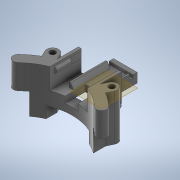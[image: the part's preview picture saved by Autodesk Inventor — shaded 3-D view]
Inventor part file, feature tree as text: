
AUTODESK INVENTOR PART (.ipt)
format: ipt  version: 2020 (Build 240168000, 168)  size: 684,544 bytes
history: native  units: mm
features: extrude x18, sketch x17, projected_geometry x14, other x6, sweep x1, chamfer x1
ambient origin geometry x8: Origin, YZ Plane, XZ Plane, XY Plane, X Axis, Y Axis, Z Axis, Center Point
bodies: Body1 (feature_tree)
feature tree (57):
  other  "Твердое тело1"
  extrude  "Выдавливание1"  Depth=35.0mm TaperAngle=0.0deg
  sketch  "Эскиз2"
  extrude  "Выдавливание2"  Depth=4.0mm
  sweep  "Сдвиг1"
  extrude  "Выдавливание5"  Depth=8.0mm
  extrude  "Выдавливание6"  Depth=35.0mm TaperAngle=0.0deg
  extrude  "Выдавливание7"  Depth=8.5mm
  extrude  "Выдавливание8"  TaperAngle=45.0deg  [1 undecoded]
  other  "РабПлоскость1"
  extrude  "Выдавливание9"  Depth=8.5mm
  extrude  "Выдавливание10"  TaperAngle=45.0deg  [1 undecoded]
  extrude  "Выдавливание11"  TaperAngle=0.0deg  [1 undecoded]
  sketch  "Эскиз13"
  other  "РабПлоскость2"
  sketch  "Эскиз14"
  extrude  "Выдавливание12"  Depth=5.0mm TaperAngle=0.0deg
  extrude  "Выдавливание13"  Depth=40.0mm TaperAngle=0.0deg
  other  "РабПлоскость3"
  extrude  "Выдавливание14"  Depth=15.0mm TaperAngle=0.0deg
  extrude  "Выдавливание15"  Depth=26.0mm
  extrude  "Выдавливание16"  Depth=6.0mm
  extrude  "Выдавливание17"  Depth=15.0mm TaperAngle=0.0deg
  chamfer  "Фаска1"  Distance=2.0mm
  other  "РабПлоскость4"
  sketch  "Эскиз18"
  extrude  "Выдавливание18"  Depth=1.5mm
  extrude  "Выдавливание19"  Depth=3.0mm
  other  "РабПлоскость5"
  extrude  "Выдавливание20"  Depth=6.0mm
  sketch  "Эскиз1"
  sketch  "Эскиз3"
  projected_geometry  "Спроецированная петля1"
  projected_geometry  "Спроецированная петля2"
  sketch  "3D эскиз1"
  sketch  "Эскиз4"
  sketch  "Эскиз6"
  projected_geometry  "Спроецированная петля4"
  sketch  "Эскиз7"
  projected_geometry  "Спроецированная петля5"
  sketch  "Эскиз9"
  projected_geometry  "Спроецированная петля7"
  sketch  "Эскиз11"
  projected_geometry  "Спроецированная петля8"
  sketch  "Эскиз12"
  projected_geometry  "Спроецированная петля9"
  projected_geometry  "Спроецированная петля10"
  sketch  "Эскиз15"
  sketch  "Эскиз16"
  projected_geometry  "Спроецированная петля11"
  projected_geometry  "Спроецированная петля12"
  sketch  "Эскиз17"
  projected_geometry  "Спроецированная петля13"
  projected_geometry  "Спроецированная петля14"
  projected_geometry  "Спроецированная петля15"
  projected_geometry  "Спроецированная петля16"
  sketch  "Эскиз19"
note: 3 required parameter values undecoded (feature->parameter linkage not recoverable at this tier; creation-order binding heuristic only, values carry confidence <= 0.55)
